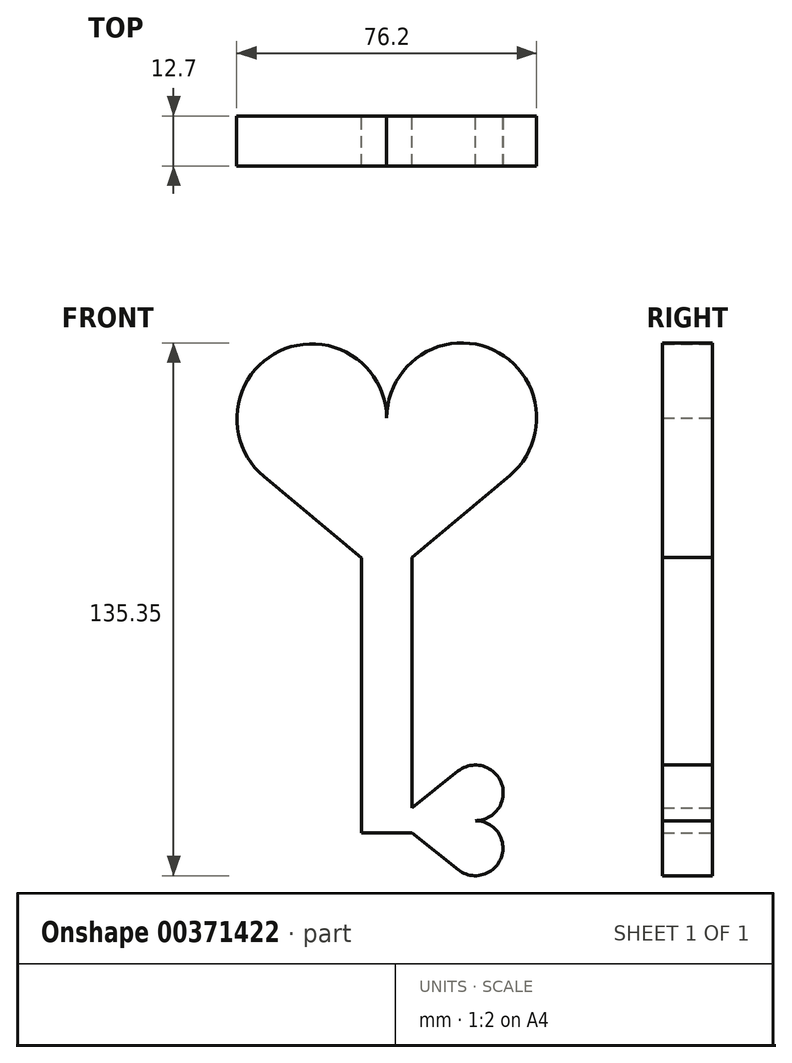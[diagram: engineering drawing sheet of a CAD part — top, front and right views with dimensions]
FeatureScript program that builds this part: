
annotation { "Feature Type Name" : "Feature", "Feature Type Description" : "" }
export const myFeature = defineFeature(function(context is Context, id is Id, definition is map)
    precondition{}
    {
        {
            var Q0;
            Q0=qCreatedBy(makeId("Front.planeOp"),FACE);
            var sketch = newSketch(context, id + "F0", { "sketchPlane" : qUnion([Q0])});
            skArc(sketch, "E0", {"start": v(0, 51.03) * mm, "mid": v(-27.25, 68) * mm, "end": v(-31.22, 36.15) * mm});
            skArc(sketch, "E1", {"start": v(31.29, 36.43) * mm, "mid": v(27.1, 68.3) * mm, "end": v(0, 51.03) * mm});
            skLineSegment(sketch, "E2", {"start": v(6.36, 15.55) * mm, "end": v(31.29, 36.43) * mm});
            skLineSegment(sketch, "E3", {"start": v(-6.36, 15.5) * mm, "end": v(-31.22, 36.15) * mm});
            skLineSegment(sketch, "E4", {"start": v(6.36, 15.55) * mm, "end": v(6.36, -48) * mm});
            skLineSegment(sketch, "E5", {"start": v(-6.36, 15.5) * mm, "end": v(-6.36, -54.35) * mm});
            skLineSegment(sketch, "E6", {"start": v(6.36, -54.4) * mm, "end": v(-6.36, -54.35) * mm});
            skArc(sketch, "E7", {"start": v(22.53, -51.3) * mm, "mid": v(29.2, -41.91) * mm, "end": v(18.15, -38.7) * mm});
            skArc(sketch, "E8", {"start": v(18.2, -63.77) * mm, "mid": v(29.13, -60.58) * mm, "end": v(22.53, -51.3) * mm});
            skLineSegment(sketch, "E9", {"start": v(6.36, -48) * mm, "end": v(18.15, -38.7) * mm});
            skLineSegment(sketch, "E10", {"start": v(6.36, -54.4) * mm, "end": v(18.2, -63.77) * mm});
            skSolve(sketch);
        }
        {
            var Q0;
            Q0=makeQuery(id+"F0.imprint","IMPRINT",FACE,{"disambiguationData":[TD([[makeQuery(id+"F0.imprint","IMPRINT",EDGE,{"derivedFrom":sQuery(id+"F0.wireOp",EDGE,"E0")}),1.0]])]});
            extrude(context, id + "F1", {"entities" : qUnion([Q0]), "depth" : 12.7 * mm});
        }
    });
